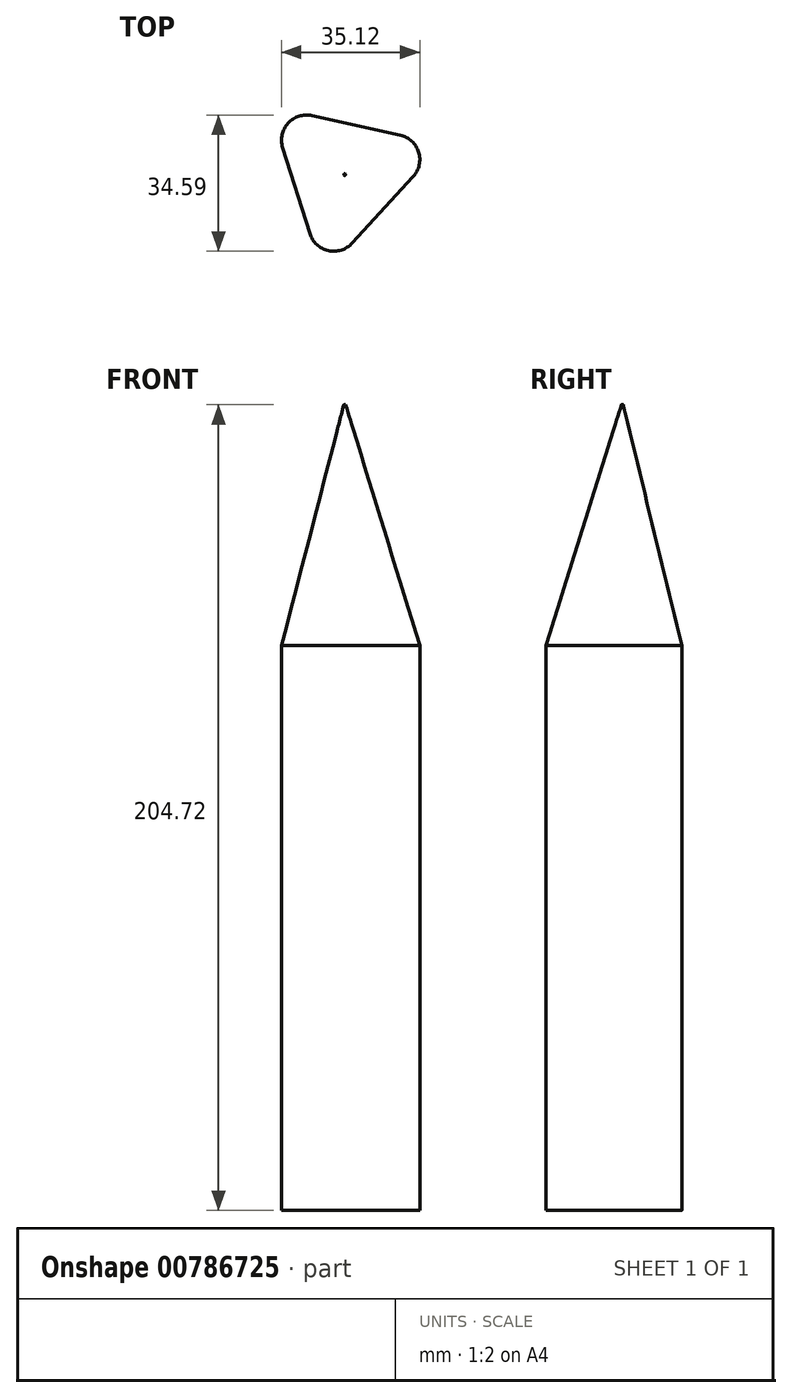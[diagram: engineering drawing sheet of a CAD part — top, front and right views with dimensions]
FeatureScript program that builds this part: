
annotation { "Feature Type Name" : "Feature", "Feature Type Description" : "" }
export const myFeature = defineFeature(function(context is Context, id is Id, definition is map)
    precondition{}
    {
        {
            var Q0;
            Q0=qCreatedBy(makeId("Top.planeOp"),FACE);
            var sketch = newSketch(context, id + "F0", { "sketchPlane" : qUnion([Q0])});
            skLineSegment(sketch, "E0.bottom", {"start": v(0, 0) * mm, "end": v(25.4, 0) * mm});
            skLineSegment(sketch, "E0.top", {"start": v(0, 25.4) * mm, "end": v(25.4, 25.4) * mm});
            skLineSegment(sketch, "E0.left", {"start": v(0, 0) * mm, "end": v(0, 25.4) * mm});
            skLineSegment(sketch, "E0.right", {"start": v(25.4, 0) * mm, "end": v(25.4, 25.4) * mm});
            skCircle(sketch, "E1", {"center": v(-24, 12.7) * mm, "radius": 18.6 * mm});
            skPoint(sketch, "E1.centerSnap0", {"position": v(0, 12.7) * mm});
            skCircle(sketch, "E2.cCircle", {"center": v(44.48, 48.07) * mm, "radius": 12.98 * mm, "construction": true});
            skLineSegment(sketch, "E2.0", {"start": v(36.08, 63.22) * mm, "end": v(58.5, 58.26) * mm});
            skLineSegment(sketch, "E2.1", {"start": v(61.8, 47.77) * mm, "end": v(46.3, 30.84) * mm});
            skLineSegment(sketch, "E2.2", {"start": v(35.56, 33.22) * mm, "end": v(28.65, 55.11) * mm});
            skPoint(sketch, "E2.0.midPoint", {"position": v(47.28, 60.74) * mm});
            skLineSegment(sketch, "E3.bottom", {"start": v(43.54, -47.09) * mm, "end": v(50.72, -47.09) * mm});
            skLineSegment(sketch, "E3.top", {"start": v(43.54, -30.6) * mm, "end": v(50.72, -30.6) * mm});
            skLineSegment(sketch, "E3.left", {"start": v(39.73, -43.28) * mm, "end": v(39.73, -34.4) * mm});
            skLineSegment(sketch, "E3.right", {"start": v(54.53, -43.28) * mm, "end": v(54.53, -34.4) * mm});
            skPoint(sketch, "E4.visualSharp", {"position": v(39.73, -47.09) * mm});
            skArc(sketch, "E4.filletArc", {"start": v(39.73, -43.28) * mm, "mid": v(40.85, -45.97) * mm, "end": v(43.54, -47.09) * mm});
            skPoint(sketch, "E5.visualSharp", {"position": v(39.73, -30.6) * mm});
            skArc(sketch, "E5.filletArc", {"start": v(43.54, -30.6) * mm, "mid": v(40.85, -31.7) * mm, "end": v(39.73, -34.4) * mm});
            skPoint(sketch, "E6.visualSharp", {"position": v(54.53, -30.6) * mm});
            skArc(sketch, "E6.filletArc", {"start": v(54.53, -34.4) * mm, "mid": v(53.42, -31.7) * mm, "end": v(50.72, -30.6) * mm});
            skPoint(sketch, "E7.visualSharp", {"position": v(54.53, -47.09) * mm});
            skArc(sketch, "E7.filletArc", {"start": v(50.72, -47.09) * mm, "mid": v(53.42, -45.97) * mm, "end": v(54.53, -43.28) * mm});
            skCircle(sketch, "E8.cCircle", {"center": v(-39.5, -45.22) * mm, "radius": 12.11 * mm, "construction": true});
            skLineSegment(sketch, "E8.0", {"start": v(-36.43, -29.82) * mm, "end": v(-23.8, -45.3) * mm});
            skLineSegment(sketch, "E8.1", {"start": v(-27.7, -55.57) * mm, "end": v(-47.42, -58.77) * mm});
            skLineSegment(sketch, "E8.2", {"start": v(-54.37, -50.25) * mm, "end": v(-47.29, -31.58) * mm});
            skPoint(sketch, "E8.0.midPoint", {"position": v(-30.12, -37.56) * mm});
            skPoint(sketch, "E9.visualSharp", {"position": v(-58.27, -60.53) * mm});
            skArc(sketch, "E9.filletArc", {"start": v(-54.37, -50.25) * mm, "mid": v(-53.35, -56.52) * mm, "end": v(-47.42, -58.77) * mm});
            skPoint(sketch, "E10.visualSharp", {"position": v(-43.38, -21.3) * mm});
            skArc(sketch, "E10.filletArc", {"start": v(-36.43, -29.82) * mm, "mid": v(-42.37, -27.57) * mm, "end": v(-47.29, -31.58) * mm});
            skPoint(sketch, "E11.visualSharp", {"position": v(-16.85, -53.81) * mm});
            skArc(sketch, "E11.filletArc", {"start": v(-27.7, -55.57) * mm, "mid": v(-22.79, -51.56) * mm, "end": v(-23.8, -45.3) * mm});
            skPoint(sketch, "E12.visualSharp", {"position": v(25.34, 65.6) * mm});
            skArc(sketch, "E12.filletArc", {"start": v(36.08, 63.22) * mm, "mid": v(30.02, 61.31) * mm, "end": v(28.65, 55.11) * mm});
            skPoint(sketch, "E13.visualSharp", {"position": v(38.87, 22.73) * mm});
            skArc(sketch, "E13.filletArc", {"start": v(35.56, 33.22) * mm, "mid": v(40.24, 28.93) * mm, "end": v(46.3, 30.84) * mm});
            skPoint(sketch, "E14.visualSharp", {"position": v(69.23, 55.89) * mm});
            skArc(sketch, "E14.filletArc", {"start": v(61.8, 47.77) * mm, "mid": v(63.18, 53.97) * mm, "end": v(58.5, 58.26) * mm});
            skSolve(sketch);
        }
        {
            var Q0;
            Q0=qCreatedBy(makeId("Top.planeOp"),FACE);
            cPlane(context, id + "F1", {"entities" : qUnion([Q0]), "cplaneType" : CPlaneType.OFFSET, "offset" : 61.2 * mm, "width" : 152.4 * mm, "height" : 152.4 * mm});
        }
        {
            var Q0;
            Q0=qCreatedBy(id+"F1.planeOp",FACE);
            var sketch = newSketch(context, id + "F2", { "sketchPlane" : qUnion([Q0])});
            skCircle(sketch, "E15", {"center": v(44.4, 48.24) * mm, "radius": 0.23 * mm});
            skSolve(sketch);
        }
        {
            var Q0;
            Q0=makeQuery(id+"F0.imprint","IMPRINT",FACE,{"disambiguationData":[TD([[makeQuery(id+"F0.imprint","IMPRINT",EDGE,{"derivedFrom":sQuery(id+"F0.wireOp",EDGE,"E2.0")}),-1.0]])]});
            var Q1;
            Q1=makeQuery(id+"F2.imprint","IMPRINT",FACE,{"disambiguationData":[TD([[makeQuery(id+"F2.imprint","IMPRINT",EDGE,{"derivedFrom":sQuery(id+"F2.wireOp",EDGE,"E15")}),1.0]])]});
            loft(context, id + "F3", {"sheetProfilesArray" : [{ "sheetProfileEntities" : qUnion([Q0]) }, { "sheetProfileEntities" : qUnion([Q1]) }]});
        }
        {
            var Q0;
            Q0=makeQuery(id+"F0.imprint","IMPRINT",FACE,{"disambiguationData":[TD([[makeQuery(id+"F0.imprint","IMPRINT",EDGE,{"derivedFrom":sQuery(id+"F0.wireOp",EDGE,"E2.0")}),-1.0]])]});
            extrude(context, id + "F4", {"entities" : qUnion([Q0]), "operationType" : NewBodyOperationType.ADD, "oppositeDirection" : true, "depth" : 143.5 * mm, "offsetDistance" : 25.4 * mm});
        }
    });
